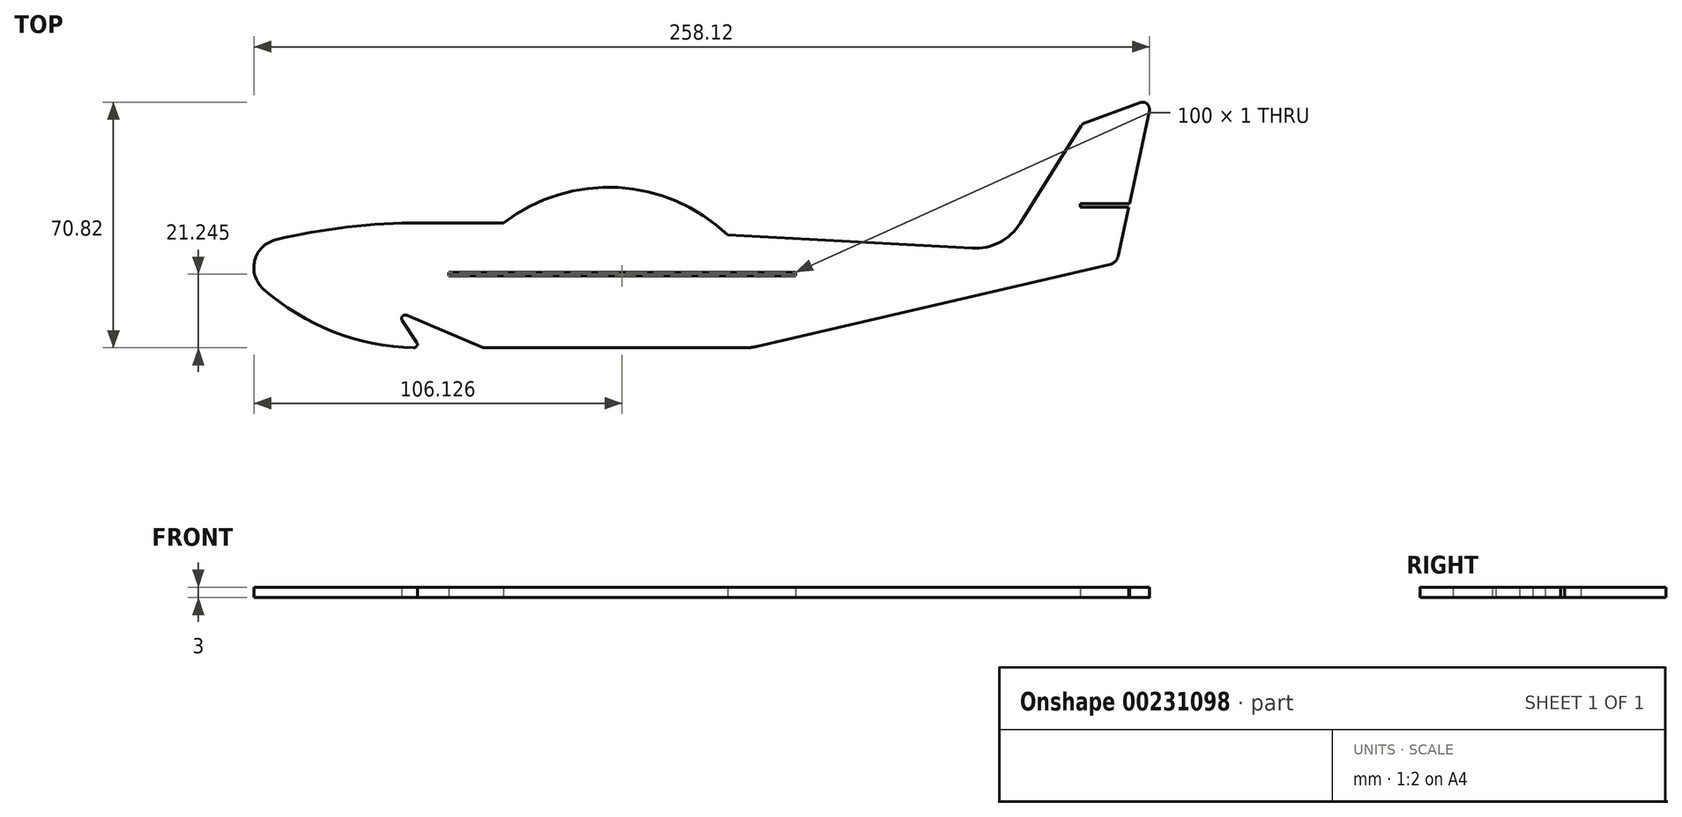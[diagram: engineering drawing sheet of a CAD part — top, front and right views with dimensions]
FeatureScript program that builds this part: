
annotation { "Feature Type Name" : "Feature", "Feature Type Description" : "" }
export const myFeature = defineFeature(function(context is Context, id is Id, definition is map)
    precondition{}
    {
        {
            var Q0;
            Q0=qCreatedBy(makeId("Top.planeOp"),FACE);
            var sketch = newSketch(context, id + "F0", { "sketchPlane" : qUnion([Q0])});
            skLineSegment(sketch, "E0", {"start": v(-49.42, 17.27) * mm, "end": v(-52.76, 17.27) * mm});
            skArc(sketch, "E1", {"start": v(-188.26, 34.23) * mm, "mid": v(-168.11, 21.92) * mm, "end": v(-144.95, 17.28) * mm});
            skLineSegment(sketch, "E2", {"start": v(-144.08, 18.88) * mm, "end": v(-148.29, 25.13) * mm});
            skLineSegment(sketch, "E3", {"start": v(-147.03, 26.65) * mm, "end": v(-124.97, 17.35) * mm});
            skArc(sketch, "E4", {"start": v(-54.45, 49.78) * mm, "mid": v(-86.11, 63.47) * mm, "end": v(-119.06, 53.26) * mm});
            skLineSegment(sketch, "E5", {"start": v(-45.92, 17.67) * mm, "end": v(55.75, 41.36) * mm});
            skLineSegment(sketch, "E6", {"start": v(29.87, 53.21) * mm, "end": v(47.42, 81.28) * mm});
            skLineSegment(sketch, "E7", {"start": v(58.06, 43.72) * mm, "end": v(61.08, 57.78) * mm});
            skLineSegment(sketch, "E8", {"start": v(64.32, 87.96) * mm, "end": v(48.45, 82.12) * mm});
            skArc(sketch, "E9", {"start": v(-147.03, 26.65) * mm, "mid": v(-148.23, 26.36) * mm, "end": v(-148.29, 25.13) * mm});
            skArc(sketch, "E10", {"start": v(-144.95, 17.28) * mm, "mid": v(-144.03, 17.82) * mm, "end": v(-144.08, 18.88) * mm});
            skArc(sketch, "E11", {"start": v(-124.97, 17.35) * mm, "mid": v(-124.77, 17.29) * mm, "end": v(-124.57, 17.27) * mm});
            skArc(sketch, "E12", {"start": v(55.75, 41.36) * mm, "mid": v(57.25, 42.2) * mm, "end": v(58.06, 43.72) * mm});
            skArc(sketch, "E13", {"start": v(-49.42, 17.27) * mm, "mid": v(-47.66, 17.37) * mm, "end": v(-45.92, 17.67) * mm});
            skArc(sketch, "E14", {"start": v(48.45, 82.12) * mm, "mid": v(47.86, 81.79) * mm, "end": v(47.42, 81.28) * mm});
            skArc(sketch, "E15", {"start": v(67.04, 85.6) * mm, "mid": v(66.38, 87.58) * mm, "end": v(64.32, 87.96) * mm});
            skLineSegment(sketch, "E16", {"start": v(-124.48, 17.27) * mm, "end": v(-124.57, 17.27) * mm});
            skLineSegment(sketch, "E17", {"start": v(-124.48, 17.27) * mm, "end": v(-52.76, 17.27) * mm});
            skLineSegment(sketch, "E18", {"start": v(47.2, 57.78) * mm, "end": v(61.08, 57.78) * mm});
            skLineSegment(sketch, "E19", {"start": v(47.2, 58.86) * mm, "end": v(61.3, 58.86) * mm});
            skLineSegment(sketch, "E20", {"start": v(47.2, 57.78) * mm, "end": v(47.2, 58.86) * mm});
            skLineSegment(sketch, "E21", {"start": v(61.3, 58.86) * mm, "end": v(67.04, 85.6) * mm});
            skArc(sketch, "E22", {"start": v(-142.97, 53.26) * mm, "mid": v(-164, 52.08) * mm, "end": v(-184.74, 48.4) * mm});
            skLineSegment(sketch, "E23", {"start": v(-119.06, 53.26) * mm, "end": v(-144.37, 53.26) * mm});
            skArc(sketch, "E24", {"start": v(-188.26, 34.23) * mm, "mid": v(-190.8, 42.38) * mm, "end": v(-184.74, 48.4) * mm});
            skLineSegment(sketch, "E25", {"start": v(-54.45, 49.78) * mm, "end": v(15.96, 45.98) * mm});
            skArc(sketch, "E26", {"start": v(15.96, 45.98) * mm, "mid": v(23.9, 47.7) * mm, "end": v(29.87, 53.21) * mm});
            skLineSegment(sketch, "E27.bottom", {"start": v(-134.91, 39.02) * mm, "end": v(-34.91, 39.02) * mm});
            skLineSegment(sketch, "E27.top", {"start": v(-134.91, 38.02) * mm, "end": v(-34.91, 38.02) * mm});
            skLineSegment(sketch, "E27.left", {"start": v(-134.91, 39.02) * mm, "end": v(-134.91, 38.02) * mm});
            skLineSegment(sketch, "E27.right", {"start": v(-34.91, 39.02) * mm, "end": v(-34.91, 38.02) * mm});
            skSolve(sketch);
        }
        {
            var Q0;
            Q0 = qSketchRegion(id + "F0", true);
            extrude(context, id + "F1", {"entities" : qUnion([Q0]), "depth" : 3 * mm});
        }
    });
